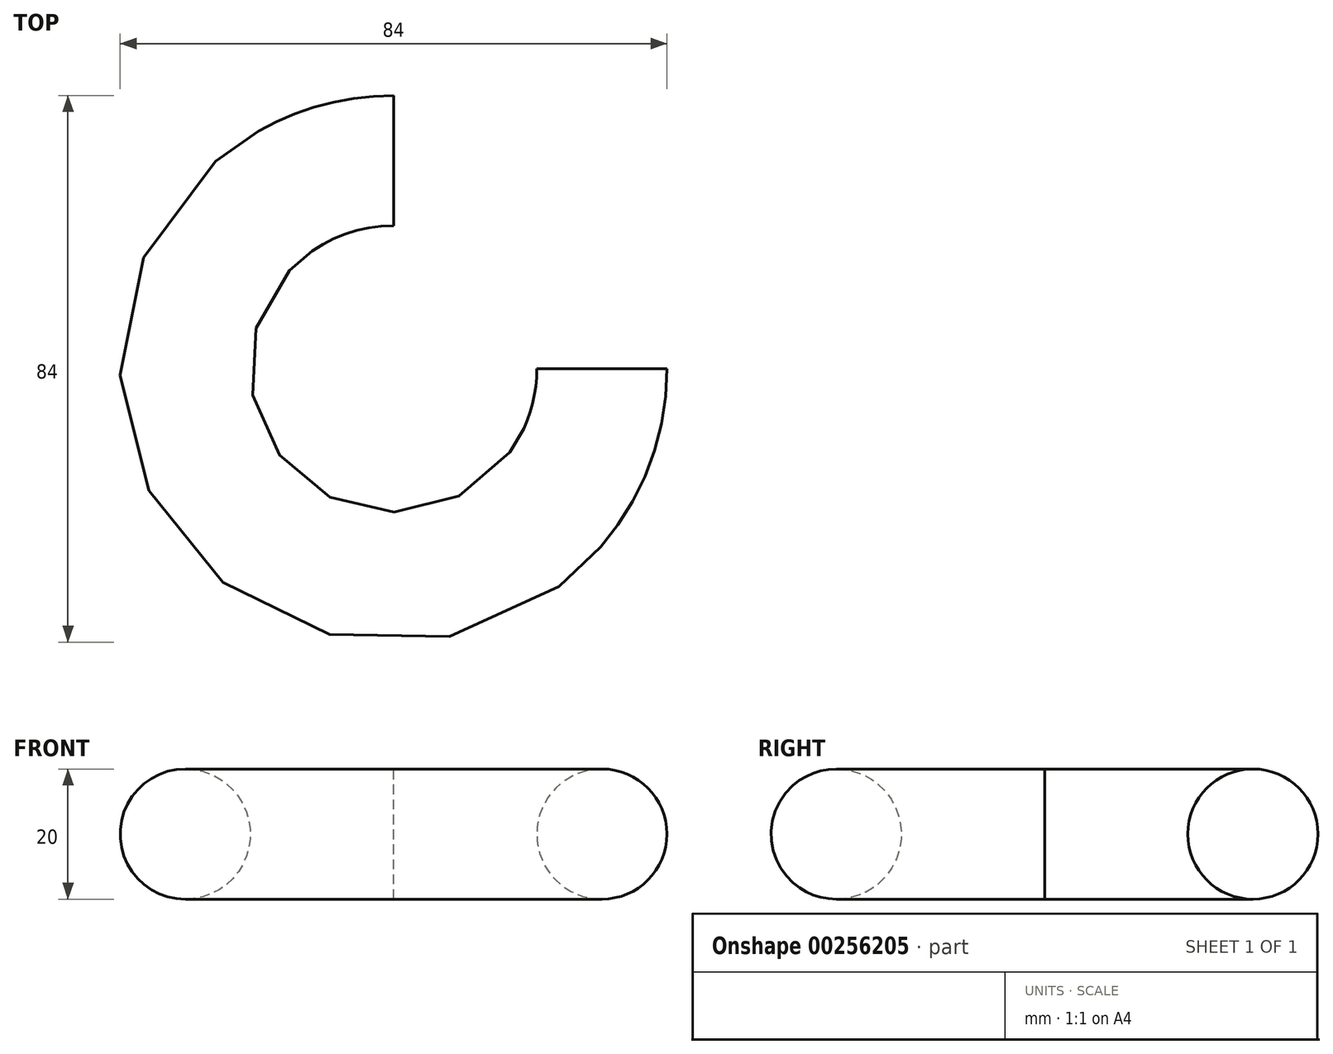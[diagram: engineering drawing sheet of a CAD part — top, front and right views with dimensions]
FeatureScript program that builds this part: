
annotation { "Feature Type Name" : "Feature", "Feature Type Description" : "" }
export const myFeature = defineFeature(function(context is Context, id is Id, definition is map)
    precondition{}
    {
        {
            var Q0;
            Q0=qCreatedBy(makeId("Front.planeOp"),FACE);
            var sketch = newSketch(context, id + "F0", { "sketchPlane" : qUnion([Q0])});
            skCircle(sketch, "E0", {"center": v(32, 0) * mm, "radius": 10 * mm});
            skLineSegment(sketch, "E1", {"start": v(0, 54.65) * mm, "end": v(0, -54.36) * mm, "construction": true});
            skSolve(sketch);
        }
        {
            var Q0;
            Q0=makeQuery(id+"F0.imprint","IMPRINT",FACE,{"disambiguationData":[TD([[makeQuery(id+"F0.imprint","IMPRINT",EDGE,{"derivedFrom":sQuery(id+"F0.wireOp",EDGE,"E0")}),1.0]])]});
            var Q1;
            Q1=sQuery(id+"F0.wireOp",EDGE,"E1");
            revolve(context, id + "F1", {"entities" : qUnion([Q0]), "axis" : qUnion([Q1]), "revolveType" : RevolveType.ONE_DIRECTION, "angle" : 270 * degree});
        }
    });
